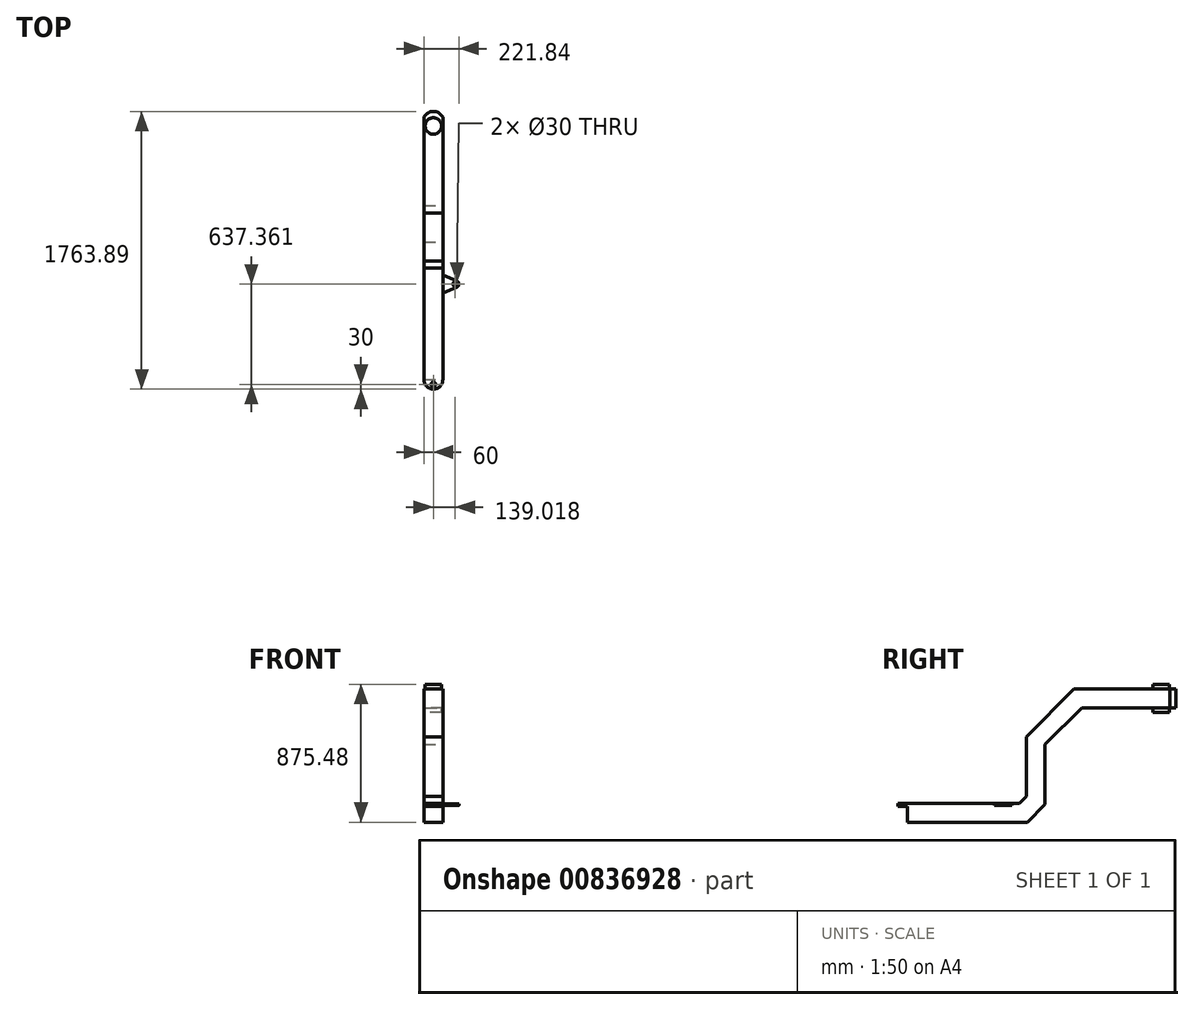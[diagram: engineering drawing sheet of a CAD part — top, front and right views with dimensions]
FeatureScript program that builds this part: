
annotation { "Feature Type Name" : "Feature", "Feature Type Description" : "" }
export const myFeature = defineFeature(function(context is Context, id is Id, definition is map)
    precondition{}
    {
        {
            var Q0;
            Q0=qCreatedBy(makeId("Right.planeOp"),FACE);
            var sketch = newSketch(context, id + "F0", { "sketchPlane" : qUnion([Q0])});
            skLineSegment(sketch, "E0", {"start": v(0, 0) * mm, "end": v(700, 0) * mm});
            skLineSegment(sketch, "E1", {"start": v(700, 0) * mm, "end": v(760, 0) * mm});
            skLineSegment(sketch, "E2", {"start": v(760, 0) * mm, "end": v(873.14, 113.14) * mm});
            skLineSegment(sketch, "E3", {"start": v(873.14, 113.14) * mm, "end": v(873.14, 493.14) * mm});
            skLineSegment(sketch, "E4", {"start": v(873.14, 493.14) * mm, "end": v(1106.48, 726.48) * mm});
            skLineSegment(sketch, "E5", {"start": v(1106.48, 726.48) * mm, "end": v(1556.48, 726.48) * mm});
            skLineSegment(sketch, "E6.0", {"start": v(1056.78, 846.48) * mm, "end": v(1556.48, 846.48) * mm});
            skLineSegment(sketch, "E6.1", {"start": v(753.14, 542.84) * mm, "end": v(1056.78, 846.48) * mm});
            skLineSegment(sketch, "E6.2", {"start": v(0, 120) * mm, "end": v(700, 120) * mm});
            skLineSegment(sketch, "E6.3", {"start": v(700, 120) * mm, "end": v(710.3, 120) * mm});
            skLineSegment(sketch, "E6.4", {"start": v(710.3, 120) * mm, "end": v(753.14, 162.84) * mm});
            skLineSegment(sketch, "E6.5", {"start": v(753.14, 162.84) * mm, "end": v(753.14, 542.84) * mm});
            skLineSegment(sketch, "E7", {"start": v(0, 120) * mm, "end": v(0, 0) * mm});
            skLineSegment(sketch, "E8", {"start": v(1556.48, 846.48) * mm, "end": v(1556.48, 726.48) * mm});
            skSolve(sketch);
        }
        {
            var Q0;
            Q0=makeQuery(id+"F0.imprint","IMPRINT",FACE,{"disambiguationData":[TD([[makeQuery(id+"F0.imprint","IMPRINT",EDGE,{"derivedFrom":sQuery(id+"F0.wireOp",EDGE,"E0")}),1.0]])]});
            extrude(context, id + "F1", {"entities" : qUnion([Q0]), "oppositeDirection" : true, "depth" : 120 * mm, "offsetDistance" : 25 * mm});
        }
        {
            var Q0;
            Q0=makeQuery(id+"F1.opExtrude","SWEPT_FACE",FACE,{"disambiguationData":[OSD([sQuery(id+"F0.wireOp",EDGE,"E6.2"),sQuery(id+"F0.wireOp",EDGE,"E6.3")])]});
            var sketch = newSketch(context, id + "F2", { "sketchPlane" : qUnion([Q0])});
            skArc(sketch, "E9", {"start": v(-120, 0) * mm, "mid": v(-60, -60) * mm, "end": v(0, 0) * mm});
            skLineSegment(sketch, "E10", {"start": v(-60, 0) * mm, "end": v(-60, -101.29) * mm, "construction": true});
            skCircle(sketch, "E11", {"center": v(-60, -30) * mm, "radius": 15 * mm});
            skLineSegment(sketch, "E12", {"start": v(-120, 0) * mm, "end": v(0, 0) * mm});
            skLineSegment(sketch, "E13", {"start": v(-60, -30) * mm, "end": v(-31.13, -30) * mm, "construction": true});
            skSolve(sketch);
        }
        {
            var Q0;
            Q0 = qSketchRegion(id + "F2", true);
            extrude(context, id + "F3", {"entities" : qUnion([Q0]), "operationType" : NewBodyOperationType.ADD, "oppositeDirection" : true, "depth" : 20 * mm, "offsetDistance" : 25 * mm});
        }
        {
            var Q0;
            Q0=qCreatedBy(makeId("Top.planeOp"),FACE);
            var Q1;
            Q1=makeQuery(id+"F2.imprint","IMPRINT",FACE,{"disambiguationData":[TD([[makeQuery(id+"F2.imprint","IMPRINT",EDGE,{"derivedFrom":sQuery(id+"F2.wireOp",EDGE,"E12")}),1.0]])]});
            cPlane(context, id + "F4", {"entities" : qUnion([Q0, Q1]), "cplaneType" : CPlaneType.MID_PLANE, "offset" : 25 * mm, "width" : 150 * mm, "height" : 150 * mm});
        }
        {
            var Q0;
            Q0=makeQuery(id+"F1.opExtrude","SWEPT_FACE",FACE,{"disambiguationData":[OSD([sQuery(id+"F0.wireOp",EDGE,"E6.0")])]});
            var sketch = newSketch(context, id + "F5", { "sketchPlane" : qUnion([Q0])});
            skLineSegment(sketch, "E14", {"start": v(-60, 1556.48) * mm, "end": v(-60, 1637.75) * mm});
            skCircle(sketch, "E15", {"center": v(-60, 1611.48) * mm, "radius": 52.5 * mm});
            skLineSegment(sketch, "E16.bottom", {"start": v(0, 1556.48) * mm, "end": v(-120, 1556.48) * mm});
            skLineSegment(sketch, "E16.top", {"start": v(0, 1666.48) * mm, "end": v(-120, 1666.48) * mm});
            skLineSegment(sketch, "E16.left", {"start": v(0, 1556.48) * mm, "end": v(0, 1666.48) * mm});
            skLineSegment(sketch, "E16.right", {"start": v(-120, 1556.48) * mm, "end": v(-120, 1666.48) * mm});
            skArc(sketch, "E17", {"start": v(0, 1666.48) * mm, "mid": v(-60, 1703.89) * mm, "end": v(-120, 1666.48) * mm});
            skSolve(sketch);
        }
        {
            var Q0;
            Q0=makeQuery(id+"F5.imprint","IMPRINT",FACE,{"disambiguationData":[TD([[makeQuery(id+"F5.imprint","IMPRINT",EDGE,{"derivedFrom":sQuery(id+"F5.wireOp",EDGE,"E15")}),-1.0]])]});
            var Q1;
            Q1=makeQuery(id+"F5.imprint","IMPRINT",FACE,{"disambiguationData":[TD([[makeQuery(id+"F5.imprint","IMPRINT",EDGE,{"derivedFrom":sQuery(id+"F5.wireOp",EDGE,"E15")}),1.0]])]});
            var Q2;
            Q2=makeQuery(id+"F5.imprint","IMPRINT",FACE,{"disambiguationData":[TD([[makeQuery(id+"F5.imprint","IMPRINT",EDGE,{"derivedFrom":sQuery(id+"F5.wireOp",EDGE,"E16.top")}),-1.0]])]});
            extrude(context, id + "F6", {"entities" : qUnion([Q0, Q1, Q2]), "operationType" : NewBodyOperationType.ADD, "oppositeDirection" : true, "depth" : 120 * mm, "offsetDistance" : 25 * mm});
        }
        {
            var Q0;
            Q0=makeQuery(id+"F5.imprint","IMPRINT",FACE,{"disambiguationData":[TD([[makeQuery(id+"F5.imprint","IMPRINT",EDGE,{"derivedFrom":sQuery(id+"F5.wireOp",EDGE,"E15")}),1.0]])]});
            extrude(context, id + "F7", {"entities" : qUnion([Q0]), "operationType" : NewBodyOperationType.ADD, "depth" : 29 * mm, "offsetDistance" : 25 * mm});
        }
        {
            var Q0;
            Q0=makeQuery(id+"F5.imprint","IMPRINT",FACE,{"disambiguationData":[TD([[makeQuery(id+"F5.imprint","IMPRINT",EDGE,{"derivedFrom":sQuery(id+"F5.wireOp",EDGE,"E15")}),1.0]])]});
            extrude(context, id + "F8", {"entities" : qUnion([Q0]), "operationType" : NewBodyOperationType.ADD, "oppositeDirection" : true, "depth" : 150 * mm, "offsetDistance" : 25 * mm});
        }
        {
            var Q0;
            Q0=makeQuery(id+"F3.boolean.opBoolean","MERGE",FACE,{"derivedFrom":[makeQuery(id+"F1.opExtrude","SWEPT_FACE",FACE,{"disambiguationData":[OSD([sQuery(id+"F0.wireOp",EDGE,"E6.2"),sQuery(id+"F0.wireOp",EDGE,"E6.3")])]}),makeQuery(id+"F3.opExtrude","CAP_FACE",FACE,{"disambiguationData":[OSD([sQuery(id+"F2.wireOp",EDGE,"E9"),sQuery(id+"F2.wireOp",EDGE,"E11"),sQuery(id+"F2.wireOp",EDGE,"E12")])],"isStart":true})]});
            var sketch = newSketch(context, id + "F9", { "sketchPlane" : qUnion([Q0])});
            skLineSegment(sketch, "E18", {"start": v(-2.97, 665.13) * mm, "end": v(89.21, 626.37) * mm});
            skLineSegment(sketch, "E19", {"start": v(89.21, 607.36) * mm, "end": v(2.97, 607.36) * mm, "construction": true});
            skLineSegment(sketch, "E20.MirrorCS", {"start": v(-2.97, 549.6) * mm, "end": v(89.21, 588.35) * mm});
            skArc(sketch, "E21", {"start": v(89.21, 588.35) * mm, "mid": v(101.84, 607.36) * mm, "end": v(89.21, 626.37) * mm});
            skLineSegment(sketch, "E22", {"start": v(79.02, 617.19) * mm, "end": v(79.02, 599.26) * mm, "construction": true});
            skCircle(sketch, "E23", {"center": v(79.02, 607.36) * mm, "radius": 15 * mm});
            skLineSegment(sketch, "E24", {"start": v(-2.97, 665.13) * mm, "end": v(-2.97, 549.6) * mm});
            skPoint(sketch, "E25.orphan", {"position": v(-9.18, 667.74) * mm});
            skPoint(sketch, "E26.orphan", {"position": v(-9.18, 546.98) * mm});
            skSolve(sketch);
        }
        {
            var Q0;
            {var subQ0=sQuery(id+"F9.wireOp",EDGE,"E24");Q0=makeQuery(id+"F9.imprint","IMPRINT",FACE,{"disambiguationData":[TD([[makeQuery(id+"F9.imprint","IMPRINT",EDGE,{"derivedFrom":subQ0}),-1.0]])]});}
            cPlane(context, id + "F10", {"entities" : qUnion([Q0]), "cplaneType" : CPlaneType.OFFSET, "offset" : 5 * mm, "oppositeDirection" : true, "width" : 150 * mm, "height" : 150 * mm});
        }
        {
            var Q0;
            Q0=qCreatedBy(id+"F10.planeOp",FACE);
            var sketch = newSketch(context, id + "F11", { "sketchPlane" : qUnion([Q0])});
            skLineSegment(sketch, "E27.0", {"start": v(-2.97, 665.13) * mm, "end": v(-2.97, 549.6) * mm});
            skLineSegment(sketch, "E27.1", {"start": v(-2.97, 665.13) * mm, "end": v(89.21, 626.37) * mm});
            skArc(sketch, "E27.2", {"start": v(89.21, 588.35) * mm, "mid": v(101.84, 607.36) * mm, "end": v(89.21, 626.37) * mm});
            skLineSegment(sketch, "E27.3", {"start": v(-2.97, 549.6) * mm, "end": v(89.21, 588.35) * mm});
            skCircle(sketch, "E27.4", {"center": v(79.02, 607.36) * mm, "radius": 15 * mm});
            skSolve(sketch);
        }
        {
            var Q0;
            Q0 = qSketchRegion(id + "F11", true);
            extrude(context, id + "F12", {"entities" : qUnion([Q0]), "operationType" : NewBodyOperationType.ADD, "oppositeDirection" : true, "depth" : 10 * mm, "offsetDistance" : 25 * mm});
        }
        {
            var Q0;
            Q0=makeQuery(id+"F12.opExtrude","CAP_FACE",FACE,{"disambiguationData":[OSD([sQuery(id+"F11.wireOp",EDGE,"E27.0"),sQuery(id+"F11.wireOp",EDGE,"E27.1"),sQuery(id+"F11.wireOp",EDGE,"E27.2"),sQuery(id+"F11.wireOp",EDGE,"E27.3"),sQuery(id+"F11.wireOp",EDGE,"E27.4")])],"isStart":true});
            cPlane(context, id + "F13", {"entities" : qUnion([Q0]), "cplaneType" : CPlaneType.OFFSET, "offset" : 35 * mm, "oppositeDirection" : true, "width" : 150 * mm, "height" : 150 * mm});
        }
    });
